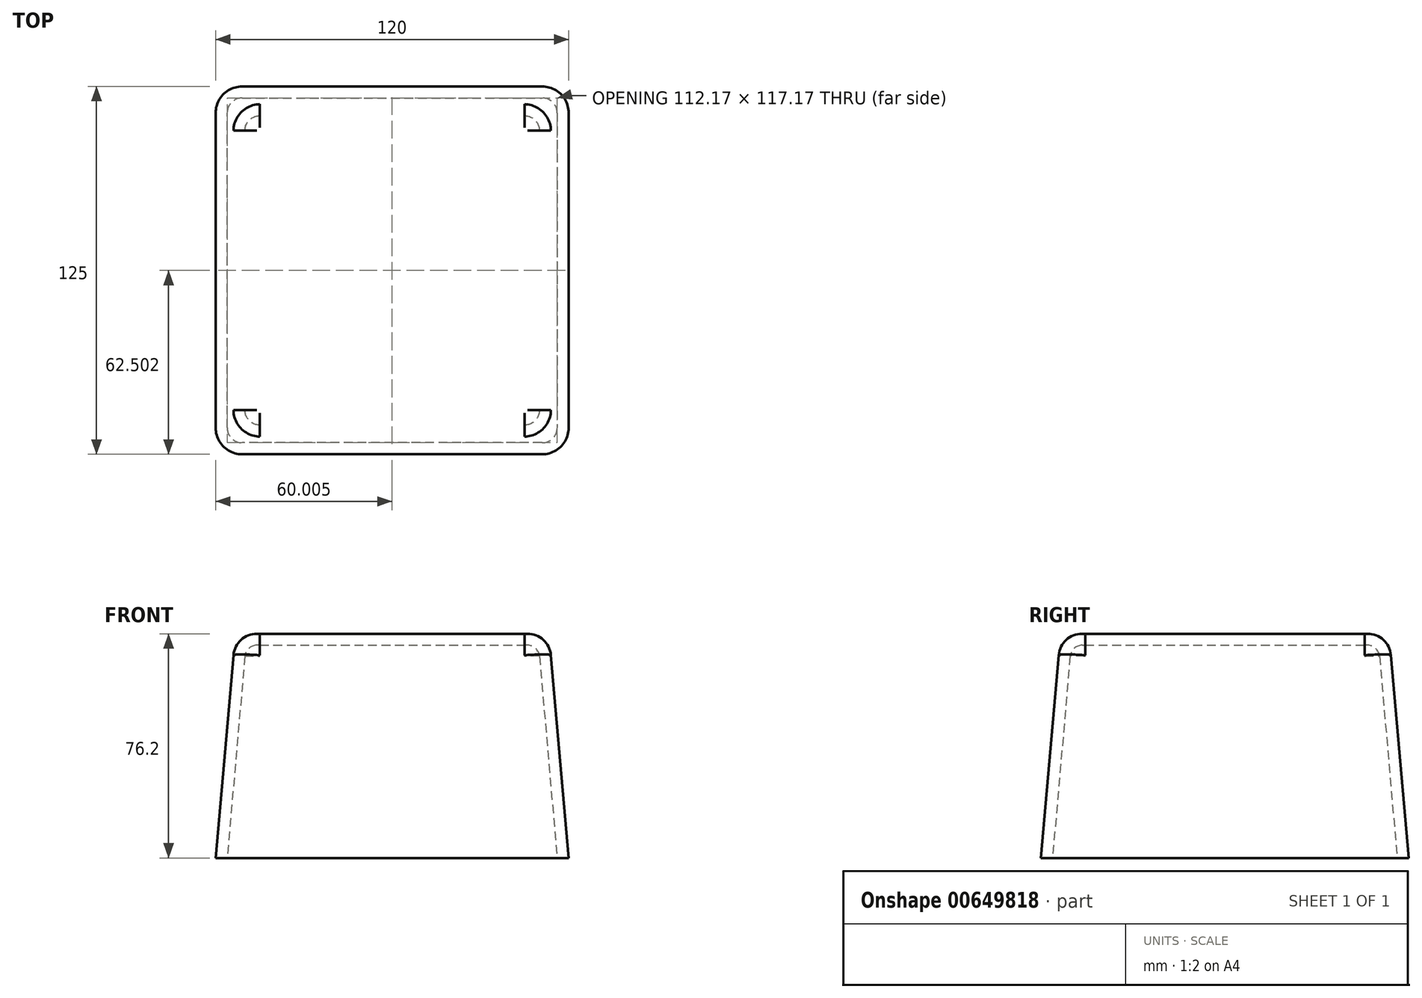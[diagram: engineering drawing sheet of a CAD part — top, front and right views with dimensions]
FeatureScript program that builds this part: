
annotation { "Feature Type Name" : "Feature", "Feature Type Description" : "" }
export const myFeature = defineFeature(function(context is Context, id is Id, definition is map)
    precondition{}
    {
        {
            var Q0;
            Q0=qCreatedBy(makeId("Top.planeOp"),FACE);
            var sketch = newSketch(context, id + "F0", { "sketchPlane" : qUnion([Q0])});
            skLineSegment(sketch, "E0.bottom", {"start": v(-49.33, 75.26) * mm, "end": v(70.67, 75.26) * mm});
            skLineSegment(sketch, "E0.top", {"start": v(-49.33, -49.74) * mm, "end": v(70.67, -49.74) * mm});
            skLineSegment(sketch, "E0.left", {"start": v(-49.33, 75.26) * mm, "end": v(-49.33, -49.74) * mm});
            skLineSegment(sketch, "E0.right", {"start": v(70.67, 75.26) * mm, "end": v(70.67, -49.74) * mm});
            skSolve(sketch);
        }
        {
            var Q0;
            Q0 = qSketchRegion(id + "F0", true);
            extrude(context, id + "F1", {"entities" : qUnion([Q0]), "depth" : 76.2 * mm, "offsetDistance" : 25.4 * mm, "hasDraft" : true, "draftAngle" : 5 * degree, "draftPullDirection" : true});
        }
        {
            var Q0;
            Q0=makeQuery(id+"F1.opExtrude","SWEPT_EDGE",EDGE,{"disambiguationData":[OSD([sQuery(id+"F0.wireOp",EDGE,"E0.bottom"),sQuery(id+"F0.wireOp",EDGE,"E0.right")])]});
            var Q1;
            Q1=makeQuery(id+"F1.opExtrude","SWEPT_EDGE",EDGE,{"disambiguationData":[OSD([sQuery(id+"F0.wireOp",EDGE,"E0.top"),sQuery(id+"F0.wireOp",EDGE,"E0.left")])]});
            var Q2;
            Q2=makeQuery(id+"F1.opExtrude","SWEPT_EDGE",EDGE,{"disambiguationData":[OSD([sQuery(id+"F0.wireOp",EDGE,"E0.bottom"),sQuery(id+"F0.wireOp",EDGE,"E0.left")])]});
            var Q3;
            Q3=makeQuery(id+"F1.opExtrude","SWEPT_EDGE",EDGE,{"disambiguationData":[OSD([sQuery(id+"F0.wireOp",EDGE,"E0.top"),sQuery(id+"F0.wireOp",EDGE,"E0.right")])]});
            fillet(context, id + "F2", {"entities" : qUnion([Q0, Q1, Q2, Q3]), "radius" : 9 * mm, "tangentPropagation" : true, "defaultsChanged" : true, "vertexSettings" : [], "allowEdgeOverflow" : false});
        }
        {
            var Q0;
            Q0=makeQuery(id+"F1.opExtrude","CAP_EDGE",EDGE,{"disambiguationData":[OSD([sQuery(id+"F0.wireOp",EDGE,"E0.top")])],"isStart":false});
            fillet(context, id + "F3", {"entities" : qUnion([Q0]), "radius" : 8 * mm, "tangentPropagation" : true, "allowEdgeOverflow" : false});
        }
        {
            var Q0;
            Q0=makeQuery(id+"F1.opExtrude","CAP_FACE",FACE,{"disambiguationData":[OSD([sQuery(id+"F0.wireOp",EDGE,"E0.bottom"),sQuery(id+"F0.wireOp",EDGE,"E0.top"),sQuery(id+"F0.wireOp",EDGE,"E0.left"),sQuery(id+"F0.wireOp",EDGE,"E0.right")])],"isStart":true});
            shell(context, id + "F4", {"entities" : qUnion([Q0]), "thickness" : 3.9 * mm});
        }
    });
